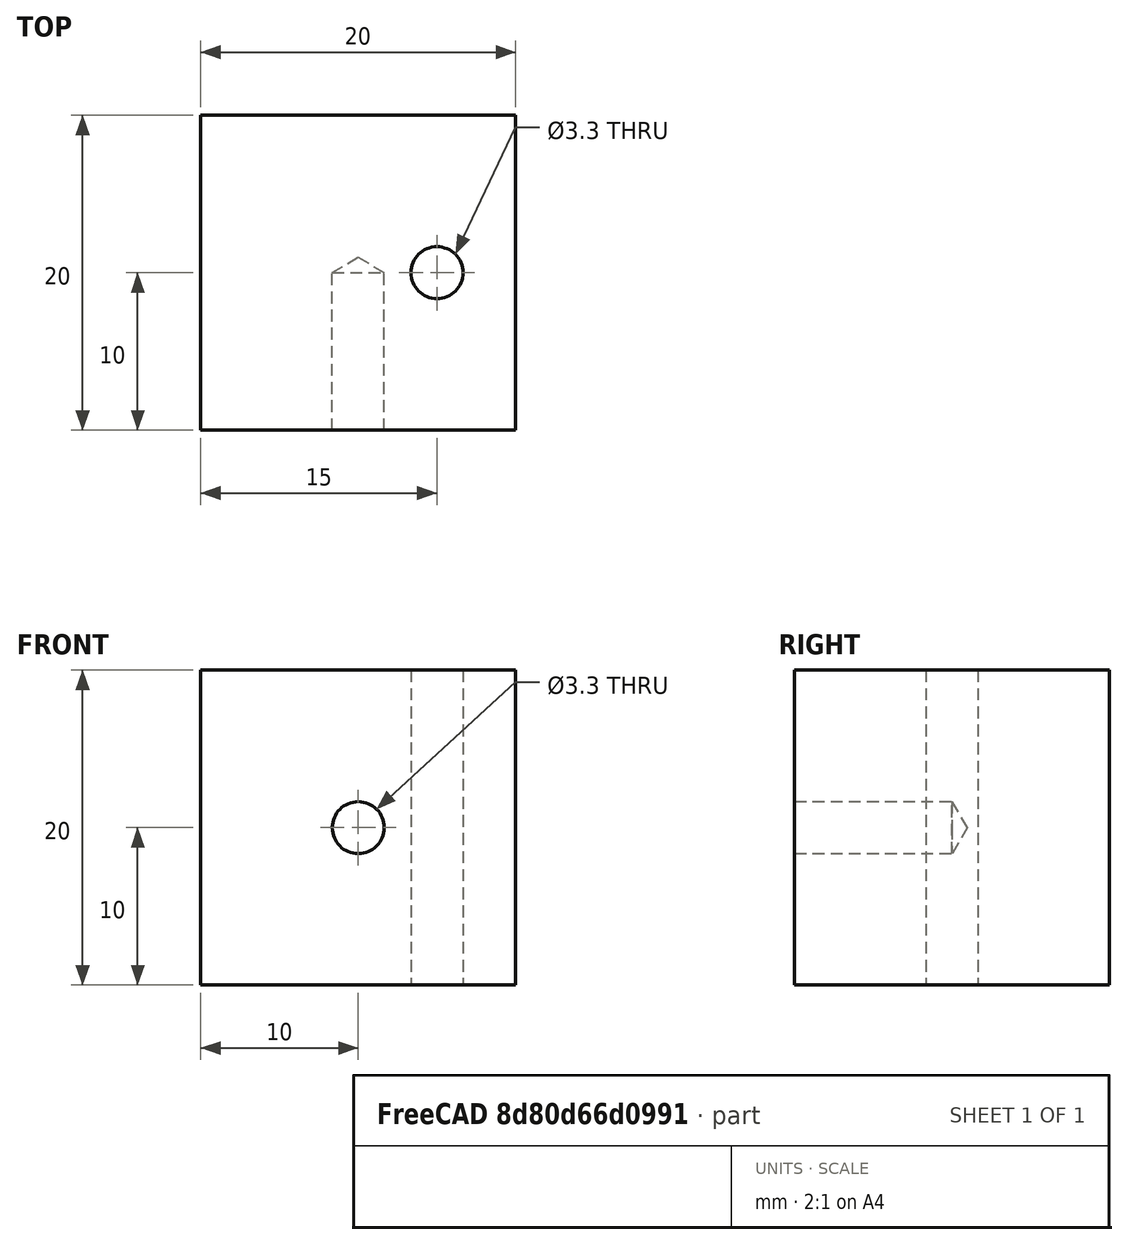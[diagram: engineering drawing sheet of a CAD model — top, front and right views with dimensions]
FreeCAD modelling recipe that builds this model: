
FCSTD DOCUMENT  (FreeCAD 1.0R39319 (Git))
Label: OCT-LBLOK-AB
License: Creative Commons Attribution 4.0
LicenseURL: https://creativecommons.org/licenses/by/4.0/
objects: TechDraw::DrawViewDimension×10, Sketcher::SketchObject×3, PartDesign::Hole×2, TechDraw::DrawProjGroupItem×2, PartDesign::Pad×1, PartDesign::Body×1, TechDraw::DrawSVGTemplate×1, TechDraw::DrawProjGroup×1, TechDraw::DrawPage×1
note: 30 computed .brp shape members not serialized (recipe doc carries the construction recipe); baked Part::Feature solids carry a one-line shape summary decoded from their .brp

FEATURE [Sketcher::SketchObject] Sketch
  ArcFitTolerance = 1e-06
  AttachmentSupport = -> [XY_Plane]
  FullyConstrained = true
  MakeInternals = false
  MapMode = 5
  sketch-geometry (4):
    g0: LineSegment StartX=-65 StartY=0 StartZ=0 EndX=-85 EndY=0 EndZ=0
    g1: LineSegment StartX=-65 StartY=20 StartZ=0 EndX=-65 EndY=0 EndZ=0
    g2: LineSegment StartX=-85 StartY=0 StartZ=0 EndX=-85 EndY=20 EndZ=0
    g3: LineSegment StartX=-65 StartY=20 StartZ=0 EndX=-85 EndY=20 EndZ=0
  constraints (12):
    c: PointOnObject(g0,g-1)
    c: PointOnObject(g0,g-1)
    c: Coincident(g1,g0)
    c: Vertical(g1)
    c: DistanceX(g0,g0) = 20
    c: DistanceY(g1,g1) = 20
    c: DistanceX(g0,g-1) = 85
    c: Coincident(g2,g0)
    c: Vertical(g2)
    c: Coincident(g3,g1)
    c: Coincident(g3,g2)
    c: Horizontal(g3)
FEATURE [PartDesign::Pad] Pad
  Direction = (0,0,1)
  Length = 20
  Length2 = 10
  Profile = -> Sketch
  ReferenceAxis = -> Sketch [N_Axis]
  Suppressed = false
  Type = 0
FEATURE [Sketcher::SketchObject] Sketch001
  ArcFitTolerance = 1e-06
  AttachmentSupport = -> [Pad]
  FullyConstrained = true
  MakeInternals = false
  MapMode = 5
  Placement = pos=(0,0,0) rot=(1,0,0;1.5708rad)
  sketch-geometry (1):
    g0: Circle CenterX=-75 CenterY=10 CenterZ=0 NormalX=0 NormalY=0 NormalZ=1 AngleXU=0 Radius=2
  constraints (3):
    c: Distance(g0,g-1) = 10
    c: Distance(g0,g-2) = 75
    c: Diameter(g0) = 4
FEATURE [PartDesign::Hole] Hole
  BaseFeature = -> Pad
  CustomThreadClearance = 0
  Depth = 10
  DepthType = 0
  Diameter = 3.3
  DrillForDepth = false
  DrillPoint = 1
  DrillPointAngle = 118
  HoleCutCountersinkAngle = 90
  HoleCutCustomValues = false
  HoleCutDepth = 0
  HoleCutDiameter = 6.1
  HoleCutType = 0
  ModelThread = false
  Profile = -> Sketch001
  Suppressed = false
  Tapered = false
  TaperedAngle = 90
  ThreadClass = 0
  ThreadDepth = 10
  ThreadDepthType = 0
  ThreadDirection = 0
  ThreadFit = 0
  ThreadSize = 11
  ThreadType = 1
  Threaded = true
  UseCustomThreadClearance = false
FEATURE [Sketcher::SketchObject] Sketch002
  ArcFitTolerance = 1e-06
  AttachmentSupport = -> [Hole]
  FullyConstrained = true
  MakeInternals = false
  MapMode = 5
  Placement = pos=(0,0,20) rot=(0,0,1;0rad)
  sketch-geometry (1):
    g0: Circle CenterX=-70 CenterY=10 CenterZ=0 NormalX=0 NormalY=0 NormalZ=1 AngleXU=0 Radius=2
  constraints (3):
    c: Diameter(g0) = 4
    c: Distance(g0,g-1) = 10
    c: Distance(g0,g-2) = 70
FEATURE [PartDesign::Hole] Hole001
  BaseFeature = -> Hole
  CustomThreadClearance = 0
  Depth = 69.9749
  DepthType = 1
  Diameter = 3.3
  DrillForDepth = false
  DrillPoint = 1
  DrillPointAngle = 118
  HoleCutCountersinkAngle = 90
  HoleCutCustomValues = false
  HoleCutDepth = 0
  HoleCutDiameter = 6.1
  HoleCutType = 0
  ModelThread = false
  Profile = -> Sketch002
  Suppressed = false
  Tapered = false
  TaperedAngle = 90
  ThreadClass = 0
  ThreadDepth = 69.9749
  ThreadDepthType = 0
  ThreadDirection = 0
  ThreadFit = 0
  ThreadSize = 11
  ThreadType = 1
  Threaded = true
  UseCustomThreadClearance = false
FEATURE [PartDesign::Body] Body  label="OCT-LBLOK-AB"
  AllowCompound = false
  Group = -> [Sketch,Pad,Sketch001,Hole,Sketch002,Hole001]
  Origin = -> Origin
  Tip = -> Hole001
FEATURE [TechDraw::DrawSVGTemplate] Template
  EditableTexts = approval_person=S. Aphelion; creator=Michael Stoll; date_of_issue=13/02/2026; document_status=In preparation; document_type=Component Drawing; drawing_number=DN; general_tolerances=ISO 2768-m; language_code=EN; part_material=Aluminium 6082 T6; responsible_department=RD; revision_index=A; scale=2 : 1; sheet_number=1 / 1; supplementary_title_1=Lower Panel Block; title=OCT-LBLOK-AB
  Height = 297
  Orientation = 1
  Template = C:/Program Files/FreeCAD 1.0/data/Mod/TechDraw/Templates/A3_Landscape_ISO5457_advanced.svg
  Width = 420
FEATURE [TechDraw::DrawProjGroupItem] View  label="Front"
  CoarseView = false
  Direction = (0,-1,0)
  Focus = 100
  HardHidden = false
  IsoCount = 0
  IsoHidden = false
  IsoVisible = false
  LockPosition = true
  Perspective = false
  Rotation = 0
  RotationVector = (1,0,0)
  Scale = 2
  ScaleType = 2
  ScrubCount = 1
  SeamHidden = false
  SeamVisible = false
  SmoothHidden = false
  SmoothVisible = true
  Source = -> [Body]
  Type = 0
  X = 0
  XDirection = (1,0,0)
  Y = 0
FEATURE [TechDraw::DrawProjGroupItem] ProjItem  label="Top"
  CoarseView = false
  Direction = (0,0,1)
  Focus = 100
  HardHidden = false
  IsoCount = 0
  IsoHidden = false
  IsoVisible = false
  LockPosition = false
  Perspective = false
  Rotation = 0
  RotationVector = (1,0,0)
  Scale = 2
  ScaleType = 0
  ScrubCount = 1
  SeamHidden = false
  SeamVisible = false
  SmoothHidden = false
  SmoothVisible = true
  Source = -> [Body]
  Type = 4
  X = 0
  XDirection = (1,0,0)
  Y = 90
FEATURE [TechDraw::DrawProjGroup] ProjGroup
  Anchor = -> View
  AutoDistribute = true
  LockPosition = false
  ProjectionType = 1
  Rotation = 0
  Scale = 2
  ScaleType = 0
  Source = -> [Body]
  Views = -> [View,ProjItem]
  X = 181.003
  Y = 115.07
  spacingX = 15
  spacingY = 50
FEATURE [TechDraw::DrawViewDimension] Dimension
  AngleOverride = false
  Arbitrary = false
  ArbitraryTolerances = false
  BoxCorners = (2) [(-20,-20,0),(20,20,0)]
  EqualTolerance = true
  ExtensionAngle = 0
  FormatSpec = %.1f
  FormatSpecOverTolerance = %+.1f
  FormatSpecUnderTolerance = %+.1f
  Inverted = false
  LineAngle = 0
  LockPosition = false
  MeasureType = 1
  OverTolerance = 0
  References2D = -> [View]
  Rotation = 0
  Scale = 2
  ScaleType = 0
  TheoreticalExact = false
  Type = 2
  UnderTolerance = 0
  X = 40.7845
  Y = 0
FEATURE [TechDraw::DrawViewDimension] Dimension001
  AngleOverride = false
  Arbitrary = false
  ArbitraryTolerances = false
  BoxCorners = (2) [(-20,-20,0),(20,20,0)]
  EqualTolerance = true
  ExtensionAngle = 0
  FormatSpec = %.1f
  FormatSpecOverTolerance = %+.1f
  FormatSpecUnderTolerance = %+.1f
  Inverted = false
  LineAngle = 0
  LockPosition = false
  MeasureType = 1
  OverTolerance = 0
  References2D = -> [View]
  Rotation = 0
  Scale = 2
  ScaleType = 0
  TheoreticalExact = false
  Type = 1
  UnderTolerance = 0
  X = 0
  Y = -36.8658
FEATURE [TechDraw::DrawViewDimension] Dimension002
  AngleOverride = false
  Arbitrary = false
  ArbitraryTolerances = false
  BoxCorners = (2) [(-20,-20,0),(20,20,0)]
  EqualTolerance = true
  ExtensionAngle = 0
  FormatSpec = %.1f
  FormatSpecOverTolerance = %+.1f
  FormatSpecUnderTolerance = %+.1f
  Inverted = false
  LineAngle = 0
  LockPosition = false
  MeasureType = 1
  OverTolerance = 0
  References2D = -> [View]
  Rotation = 0
  Scale = 2
  ScaleType = 0
  TheoreticalExact = false
  Type = 0
  UnderTolerance = 0
  X = -46.1057
  Y = -10
FEATURE [TechDraw::DrawViewDimension] Dimension003
  AngleOverride = false
  Arbitrary = false
  ArbitraryTolerances = false
  BoxCorners = (2) [(-20,-20,0),(20,20,0)]
  EqualTolerance = true
  ExtensionAngle = 0
  FormatSpec = %.1f
  FormatSpecOverTolerance = %+.1f
  FormatSpecUnderTolerance = %+.1f
  Inverted = false
  LineAngle = 0
  LockPosition = false
  MeasureType = 1
  OverTolerance = 0
  References2D = -> [View]
  Rotation = 0
  Scale = 2
  ScaleType = 0
  TheoreticalExact = false
  Type = 0
  UnderTolerance = 0
  X = 10
  Y = 39.2356
FEATURE [TechDraw::DrawViewDimension] Dimension004
  AngleOverride = false
  Arbitrary = false
  ArbitraryTolerances = false
  BoxCorners = (2) [(-20,-20,0),(20,20,0)]
  EqualTolerance = true
  ExtensionAngle = 0
  FormatSpec = %.1f
  FormatSpecOverTolerance = %+.1f
  FormatSpecUnderTolerance = %+.1f
  Inverted = false
  LineAngle = 0
  LockPosition = false
  MeasureType = 1
  OverTolerance = 0
  References2D = -> [ProjItem]
  Rotation = 0
  Scale = 2
  ScaleType = 0
  TheoreticalExact = false
  Type = 2
  UnderTolerance = 0
  X = 50.7236
  Y = 0
FEATURE [TechDraw::DrawViewDimension] Dimension005
  AngleOverride = false
  Arbitrary = false
  ArbitraryTolerances = false
  BoxCorners = (2) [(-20,-20,0),(20,20,0)]
  EqualTolerance = true
  ExtensionAngle = 0
  FormatSpec = %.1f
  FormatSpecOverTolerance = %+.1f
  FormatSpecUnderTolerance = %+.1f
  Inverted = false
  LineAngle = 0
  LockPosition = false
  MeasureType = 1
  OverTolerance = 0
  References2D = -> [ProjItem]
  Rotation = 0
  Scale = 2
  ScaleType = 0
  TheoreticalExact = false
  Type = 2
  UnderTolerance = 0
  X = -60.5712
  Y = 0
FEATURE [TechDraw::DrawViewDimension] Dimension011
  AngleOverride = false
  Arbitrary = false
  ArbitraryTolerances = false
  BoxCorners = (2) [(-20,-20,0),(20,20,0)]
  EqualTolerance = true
  ExtensionAngle = 0
  FormatSpec = ⌀%.1f
  FormatSpecOverTolerance = %+.1f
  FormatSpecUnderTolerance = %+.1f
  Inverted = false
  LineAngle = 0
  LockPosition = false
  MeasureType = 1
  OverTolerance = 0
  References2D = -> [View]
  Rotation = 0
  Scale = 2
  ScaleType = 0
  TheoreticalExact = false
  Type = 5
  UnderTolerance = 0
  X = -40.3396
  Y = 24.9886
FEATURE [TechDraw::DrawViewDimension] Dimension012
  AngleOverride = false
  Arbitrary = false
  ArbitraryTolerances = false
  BoxCorners = (2) [(-20,-20,0),(20,20,0)]
  EqualTolerance = true
  ExtensionAngle = 0
  FormatSpec = %.1f
  FormatSpecOverTolerance = %+.1f
  FormatSpecUnderTolerance = %+.1f
  Inverted = false
  LineAngle = 0
  LockPosition = false
  MeasureType = 1
  OverTolerance = 0
  References2D = -> [ProjItem]
  Rotation = 0
  Scale = 2
  ScaleType = 0
  TheoreticalExact = false
  Type = 0
  UnderTolerance = 0
  X = 15
  Y = 41.2261
FEATURE [TechDraw::DrawViewDimension] Dimension013
  AngleOverride = false
  Arbitrary = false
  ArbitraryTolerances = false
  BoxCorners = (2) [(-20,-20,0),(20,20,0)]
  EqualTolerance = true
  ExtensionAngle = 0
  FormatSpec = %.1f
  FormatSpecOverTolerance = %+.1f
  FormatSpecUnderTolerance = %+.1f
  Inverted = false
  LineAngle = 0
  LockPosition = false
  MeasureType = 1
  OverTolerance = 0
  References2D = -> [ProjItem]
  Rotation = 0
  Scale = 2
  ScaleType = 0
  TheoreticalExact = false
  Type = 0
  UnderTolerance = 0
  X = 27.5483
  Y = -10
FEATURE [TechDraw::DrawViewDimension] Dimension014
  AngleOverride = false
  Arbitrary = false
  ArbitraryTolerances = false
  BoxCorners = (2) [(-20,-20,0),(20,20,0)]
  EqualTolerance = true
  ExtensionAngle = 0
  FormatSpec = ⌀%.1f
  FormatSpecOverTolerance = %+.1f
  FormatSpecUnderTolerance = %+.1f
  Inverted = false
  LineAngle = 0
  LockPosition = false
  MeasureType = 1
  OverTolerance = 0
  References2D = -> [ProjItem]
  Rotation = 0
  Scale = 2
  ScaleType = 0
  TheoreticalExact = false
  Type = 5
  UnderTolerance = 0
  X = -22.8793
  Y = 47.2125
FEATURE [TechDraw::DrawPage] Page
  KeepUpdated = true
  NextBalloonIndex = 1
  ProjectionType = 1
  Scale = 2
  Template = -> Template
  Views = -> [ProjGroup,Dimension,Dimension001,Dimension002,Dimension003,Dimension004,Dimension005,Dimension011,Dimension012,Dimension013,Dimension014]
